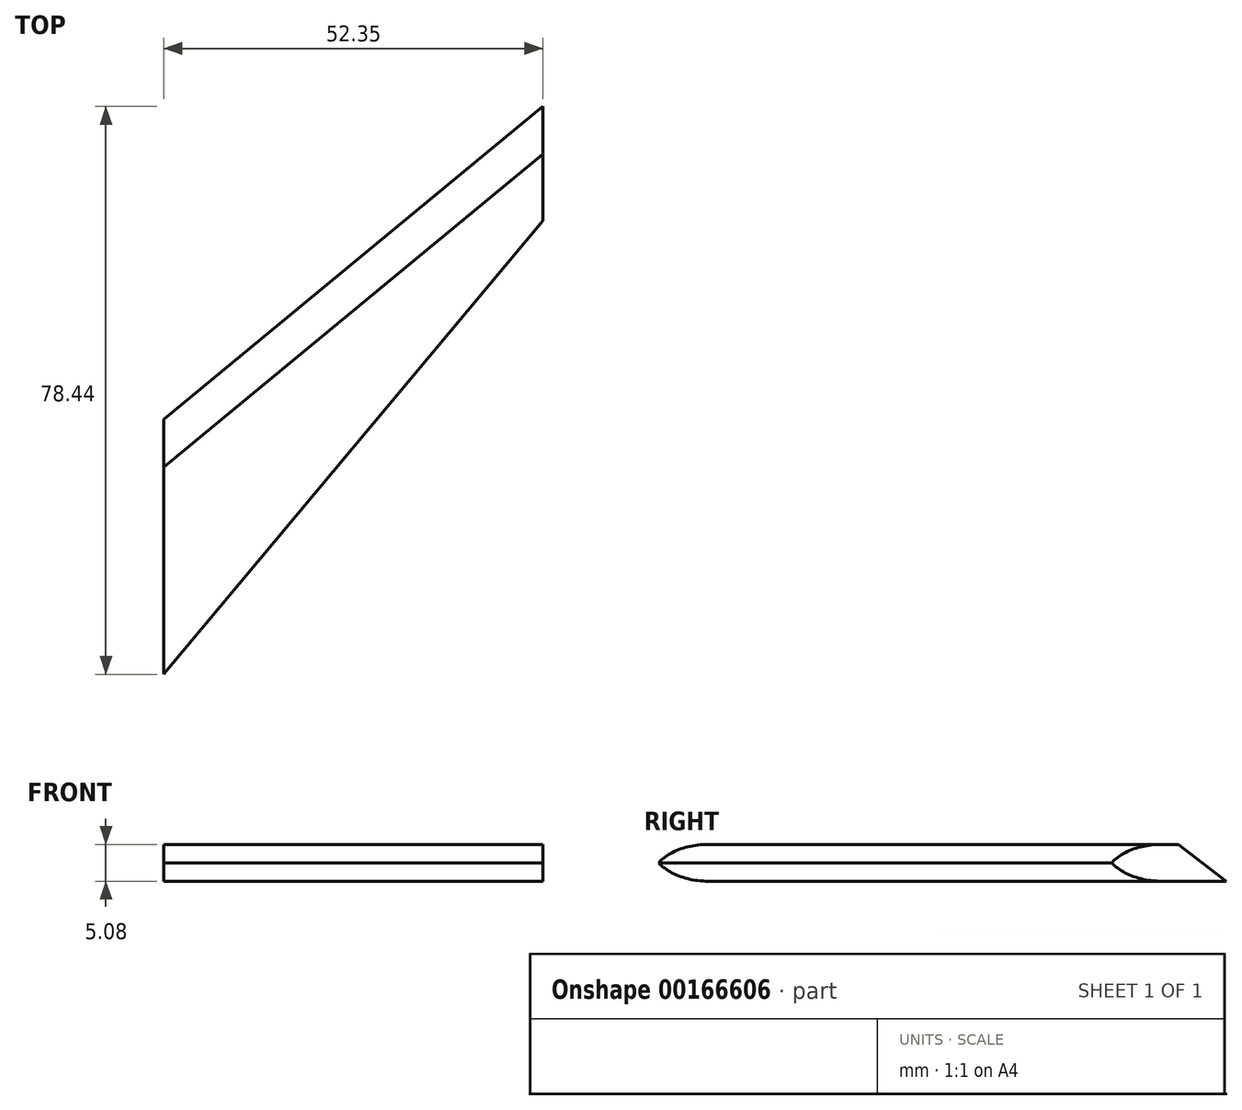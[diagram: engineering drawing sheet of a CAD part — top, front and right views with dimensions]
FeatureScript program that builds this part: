
annotation { "Feature Type Name" : "Feature", "Feature Type Description" : "" }
export const myFeature = defineFeature(function(context is Context, id is Id, definition is map)
    precondition{}
    {
        {
            var Q0;
            Q0=qCreatedBy(makeId("Top.planeOp"),FACE);
            var sketch = newSketch(context, id + "F0", { "sketchPlane" : qUnion([Q0])});
            skLineSegment(sketch, "E0", {"start": v(0, 0) * mm, "end": v(0, 36.28) * mm});
            skLineSegment(sketch, "E1", {"start": v(52.35, 79.5) * mm, "end": v(52.35, 62.62) * mm});
            skLineSegment(sketch, "E2", {"start": v(52.35, 62.62) * mm, "end": v(0, 0) * mm});
            skLineSegment(sketch, "E3", {"start": v(0, 36.28) * mm, "end": v(52.35, 79.5) * mm});
            skSolve(sketch);
        }
        {
            var Q0;
            Q0=makeQuery(id+"F0.imprint","IMPRINT",FACE,{"disambiguationData":[TD([[makeQuery(id+"F0.imprint","IMPRINT",EDGE,{"derivedFrom":sQuery(id+"F0.wireOp",EDGE,"E0")}),-1.0]])]});
            extrude(context, id + "F1", {"entities" : qUnion([Q0]), "depth" : 5.08 * mm});
        }
        {
            var Q0;
            Q0=makeQuery(id+"F1.opExtrude","CAP_EDGE",EDGE,{"disambiguationData":[OSD([sQuery(id+"F0.wireOp",EDGE,"E2")])],"isStart":false});
            var Q1;
            Q1=makeQuery(id+"F1.opExtrude","CAP_EDGE",EDGE,{"disambiguationData":[OSD([sQuery(id+"F0.wireOp",EDGE,"E2")])],"isStart":true});
            fillet(context, id + "F2", {"entities" : qUnion([Q0, Q1]), "radius" : 5.08 * mm, "tangentPropagation" : true, "allowEdgeOverflow" : false});
        }
        {
            var Q0;
            Q0=makeQuery(id+"F1.opExtrude","CAP_EDGE",EDGE,{"disambiguationData":[OSD([sQuery(id+"F0.wireOp",EDGE,"E3")])],"isStart":false});
            chamfer(context, id + "F3", {"entities" : qUnion([Q0]), "width" : 5.08 * mm, "tangentPropagation" : true});
        }
    });
